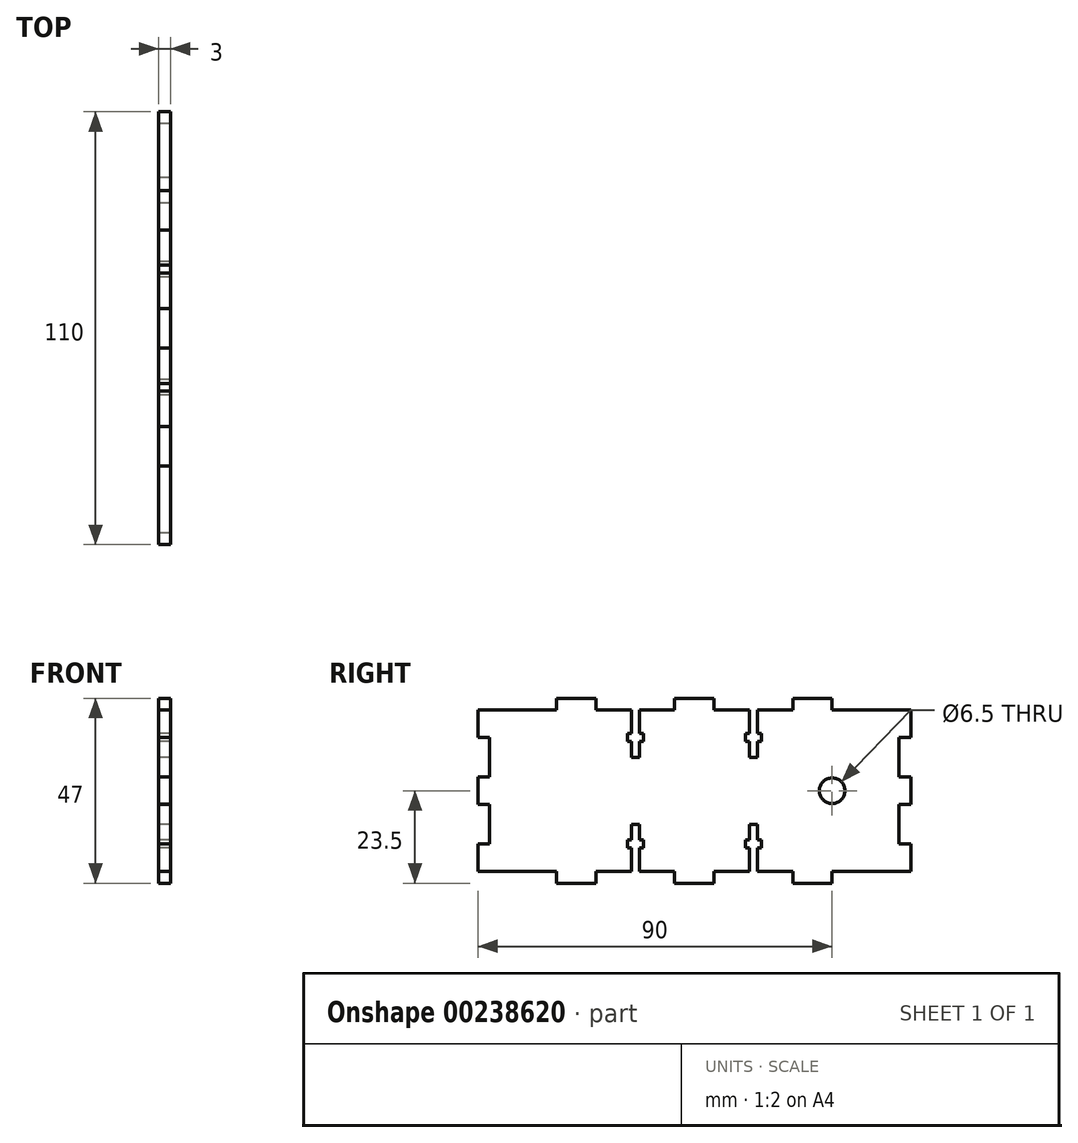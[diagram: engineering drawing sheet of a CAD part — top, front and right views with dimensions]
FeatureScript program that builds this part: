
annotation { "Feature Type Name" : "Feature", "Feature Type Description" : "" }
export const myFeature = defineFeature(function(context is Context, id is Id, definition is map)
    precondition{}
    {
        {
            var Q0;
            Q0=qCreatedBy(makeId("Right.planeOp"),FACE);
            var sketch = newSketch(context, id + "F0", { "sketchPlane" : qUnion([Q0])});
            skLineSegment(sketch, "E0", {"start": v(0, 0) * mm, "end": v(0, 3) * mm});
            skLineSegment(sketch, "E1", {"start": v(0, 3) * mm, "end": v(17, 3) * mm});
            skLineSegment(sketch, "E2", {"start": v(17, 3) * mm, "end": v(17, 10) * mm});
            skLineSegment(sketch, "E3", {"start": v(17, 10) * mm, "end": v(14, 10) * mm});
            skLineSegment(sketch, "E4", {"start": v(14, 10) * mm, "end": v(14, 20) * mm});
            skLineSegment(sketch, "E5", {"start": v(14, 20) * mm, "end": v(17, 20) * mm});
            skLineSegment(sketch, "E6", {"start": v(17, 20) * mm, "end": v(17, 27) * mm});
            skLineSegment(sketch, "E7", {"start": v(17, 27) * mm, "end": v(14, 27) * mm});
            skLineSegment(sketch, "E8", {"start": v(14, 27) * mm, "end": v(14, 37) * mm});
            skLineSegment(sketch, "E9", {"start": v(14, 37) * mm, "end": v(17, 37) * mm});
            skLineSegment(sketch, "E10", {"start": v(17, 37) * mm, "end": v(17, 44) * mm});
            skLineSegment(sketch, "E11", {"start": v(17, 44) * mm, "end": v(-3, 44) * mm});
            skLineSegment(sketch, "E12", {"start": v(-3, 44) * mm, "end": v(-3, 47) * mm});
            skLineSegment(sketch, "E13", {"start": v(-3, 47) * mm, "end": v(-13, 47) * mm});
            skLineSegment(sketch, "E14", {"start": v(-13, 47) * mm, "end": v(-13, 44) * mm});
            skLineSegment(sketch, "E15", {"start": v(-13, 44) * mm, "end": v(-22, 44) * mm});
            skLineSegment(sketch, "E16", {"start": v(-33, 44) * mm, "end": v(-33, 47) * mm});
            skLineSegment(sketch, "E17", {"start": v(-33, 47) * mm, "end": v(-43, 47) * mm});
            skLineSegment(sketch, "E18", {"start": v(-43, 47) * mm, "end": v(-43, 44) * mm});
            skLineSegment(sketch, "E19", {"start": v(-43, 44) * mm, "end": v(-52, 44) * mm});
            skLineSegment(sketch, "E20", {"start": v(-63, 44) * mm, "end": v(-63, 47) * mm});
            skLineSegment(sketch, "E21", {"start": v(-63, 47) * mm, "end": v(-73, 47) * mm});
            skLineSegment(sketch, "E22", {"start": v(-73, 47) * mm, "end": v(-73, 44) * mm});
            skLineSegment(sketch, "E23", {"start": v(-73, 44) * mm, "end": v(-93, 44) * mm});
            skLineSegment(sketch, "E24", {"start": v(17, 23.5) * mm, "end": v(-102.63, 23.5) * mm, "construction": true});
            skLineSegment(sketch, "E25.MirrorCS", {"start": v(-33, 3) * mm, "end": v(-33, 0) * mm});
            skLineSegment(sketch, "E26.MirrorCS", {"start": v(-43, 0) * mm, "end": v(-43, 3) * mm});
            skLineSegment(sketch, "E27.MirrorCS", {"start": v(-63, 3) * mm, "end": v(-63, 0) * mm});
            skLineSegment(sketch, "E28.MirrorCS", {"start": v(-73, 0) * mm, "end": v(-73, 3) * mm});
            skLineSegment(sketch, "E29.MirrorCS", {"start": v(-3, 3) * mm, "end": v(-3, 0) * mm});
            skLineSegment(sketch, "E30.MirrorCS", {"start": v(-13, 0) * mm, "end": v(-13, 3) * mm});
            skLineSegment(sketch, "E31.MirrorCS", {"start": v(17, 3) * mm, "end": v(-3, 3) * mm});
            skLineSegment(sketch, "E32.MirrorCS", {"start": v(-63, 0) * mm, "end": v(-73, 0) * mm});
            skLineSegment(sketch, "E33.MirrorCS", {"start": v(-43, 3) * mm, "end": v(-52, 3) * mm});
            skLineSegment(sketch, "E34.MirrorCS", {"start": v(-73, 3) * mm, "end": v(-93, 3) * mm});
            skLineSegment(sketch, "E35.MirrorCS", {"start": v(-3, 0) * mm, "end": v(-13, 0) * mm});
            skLineSegment(sketch, "E36.MirrorCS", {"start": v(-13, 3) * mm, "end": v(-22, 3) * mm});
            skLineSegment(sketch, "E37.MirrorCS", {"start": v(-33, 0) * mm, "end": v(-43, 0) * mm});
            skLineSegment(sketch, "E38", {"start": v(-38, 47) * mm, "end": v(-38, 0) * mm, "construction": true});
            skLineSegment(sketch, "E39.MirrorCS", {"start": v(-90, 37) * mm, "end": v(-93, 37) * mm});
            skLineSegment(sketch, "E40.MirrorCS", {"start": v(-93, 27) * mm, "end": v(-90, 27) * mm});
            skLineSegment(sketch, "E41.MirrorCS", {"start": v(-90, 20) * mm, "end": v(-93, 20) * mm});
            skLineSegment(sketch, "E42.MirrorCS", {"start": v(-93, 10) * mm, "end": v(-90, 10) * mm});
            skLineSegment(sketch, "E43.MirrorCS", {"start": v(-93, 20) * mm, "end": v(-93, 27) * mm});
            skLineSegment(sketch, "E44.MirrorCS", {"start": v(-90, 27) * mm, "end": v(-90, 37) * mm});
            skLineSegment(sketch, "E45.MirrorCS", {"start": v(-93, 37) * mm, "end": v(-93, 44) * mm});
            skLineSegment(sketch, "E46.MirrorCS", {"start": v(-93, 3) * mm, "end": v(-93, 10) * mm});
            skLineSegment(sketch, "E47.MirrorCS", {"start": v(-90, 10) * mm, "end": v(-90, 20) * mm});
            skLineSegment(sketch, "E48", {"start": v(-23, 44) * mm, "end": v(-23, 38) * mm, "construction": true});
            skLineSegment(sketch, "E49.left", {"start": v(-24, 44) * mm, "end": v(-24, 38) * mm});
            skLineSegment(sketch, "E49.right", {"start": v(-22, 44) * mm, "end": v(-22, 38) * mm});
            skLineSegment(sketch, "E50.trimOffspring", {"start": v(-24, 44) * mm, "end": v(-33, 44) * mm});
            skLineSegment(sketch, "E51.bottom", {"start": v(-25, 38) * mm, "end": v(-24, 38) * mm});
            skLineSegment(sketch, "E51.top", {"start": v(-25, 36) * mm, "end": v(-24, 36) * mm});
            skLineSegment(sketch, "E51.left", {"start": v(-25, 38) * mm, "end": v(-25, 36) * mm});
            skLineSegment(sketch, "E51.right", {"start": v(-21, 38) * mm, "end": v(-21, 36) * mm});
            skLineSegment(sketch, "E52.trimOffspring", {"start": v(-22, 38) * mm, "end": v(-21, 38) * mm});
            skLineSegment(sketch, "E53.trimOffspring", {"start": v(-24, 36) * mm, "end": v(-24, 32) * mm});
            skLineSegment(sketch, "E54.trimOffspring", {"start": v(-22, 36) * mm, "end": v(-21, 36) * mm});
            skLineSegment(sketch, "E55.trimOffspring", {"start": v(-23, 36) * mm, "end": v(-23, 13.38) * mm, "construction": true});
            skLineSegment(sketch, "E56.trimOffspring", {"start": v(-22, 36) * mm, "end": v(-22, 32) * mm});
            skLineSegment(sketch, "E57.MirrorCS", {"start": v(-51, 36) * mm, "end": v(-52, 36) * mm});
            skLineSegment(sketch, "E58.MirrorCS", {"start": v(-54, 38) * mm, "end": v(-55, 38) * mm});
            skLineSegment(sketch, "E59.MirrorCS", {"start": v(-51, 38) * mm, "end": v(-51, 36) * mm});
            skLineSegment(sketch, "E60.MirrorCS", {"start": v(-54, 36) * mm, "end": v(-55, 36) * mm});
            skLineSegment(sketch, "E61.MirrorCS", {"start": v(-51, 38) * mm, "end": v(-52, 38) * mm});
            skLineSegment(sketch, "E62.MirrorCS", {"start": v(-55, 38) * mm, "end": v(-55, 36) * mm});
            skLineSegment(sketch, "E63.MirrorCS", {"start": v(-52, 44) * mm, "end": v(-52, 38) * mm});
            skLineSegment(sketch, "E64.MirrorCS", {"start": v(-54, 44) * mm, "end": v(-54, 38) * mm});
            skLineSegment(sketch, "E65.MirrorCS", {"start": v(-54, 36) * mm, "end": v(-54, 32) * mm});
            skLineSegment(sketch, "E66.MirrorCS", {"start": v(-53, 44) * mm, "end": v(-53, 38) * mm, "construction": true});
            skLineSegment(sketch, "E67.MirrorCS", {"start": v(-52, 36) * mm, "end": v(-52, 32) * mm});
            skLineSegment(sketch, "E68", {"start": v(-24, 32) * mm, "end": v(-22, 32) * mm});
            skLineSegment(sketch, "E69", {"start": v(-54, 32) * mm, "end": v(-52, 32) * mm});
            skLineSegment(sketch, "E70.trimOffspring", {"start": v(-54, 44) * mm, "end": v(-63, 44) * mm});
            skLineSegment(sketch, "E71.MirrorCS", {"start": v(-22, 11) * mm, "end": v(-21, 11) * mm});
            skLineSegment(sketch, "E72.MirrorCS", {"start": v(-51, 9) * mm, "end": v(-52, 9) * mm});
            skLineSegment(sketch, "E73.MirrorCS", {"start": v(-22, 9) * mm, "end": v(-21, 9) * mm});
            skLineSegment(sketch, "E74.MirrorCS", {"start": v(-21, 9) * mm, "end": v(-21, 11) * mm});
            skLineSegment(sketch, "E75.MirrorCS", {"start": v(-55, 9) * mm, "end": v(-55, 11) * mm});
            skLineSegment(sketch, "E76.MirrorCS", {"start": v(-54, 15) * mm, "end": v(-52, 15) * mm});
            skLineSegment(sketch, "E77.MirrorCS", {"start": v(-25, 9) * mm, "end": v(-25, 11) * mm});
            skLineSegment(sketch, "E78.MirrorCS", {"start": v(-51, 9) * mm, "end": v(-51, 11) * mm});
            skLineSegment(sketch, "E79.MirrorCS", {"start": v(-54, 11) * mm, "end": v(-55, 11) * mm});
            skLineSegment(sketch, "E80.MirrorCS", {"start": v(-25, 9) * mm, "end": v(-24, 9) * mm});
            skLineSegment(sketch, "E81.MirrorCS", {"start": v(-24, 15) * mm, "end": v(-22, 15) * mm});
            skLineSegment(sketch, "E82.MirrorCS", {"start": v(-51, 11) * mm, "end": v(-52, 11) * mm});
            skLineSegment(sketch, "E83.MirrorCS", {"start": v(-54, 9) * mm, "end": v(-55, 9) * mm});
            skLineSegment(sketch, "E84.MirrorCS", {"start": v(-25, 11) * mm, "end": v(-24, 11) * mm});
            skLineSegment(sketch, "E85.MirrorCS", {"start": v(-52, 3) * mm, "end": v(-52, 9) * mm});
            skLineSegment(sketch, "E86.MirrorCS", {"start": v(-24, 3) * mm, "end": v(-33, 3) * mm});
            skLineSegment(sketch, "E87.MirrorCS", {"start": v(-22, 3) * mm, "end": v(-22, 9) * mm});
            skLineSegment(sketch, "E88.MirrorCS", {"start": v(-24, 11) * mm, "end": v(-24, 15) * mm});
            skLineSegment(sketch, "E89.MirrorCS", {"start": v(-53, 3) * mm, "end": v(-53, 9) * mm, "construction": true});
            skLineSegment(sketch, "E90.MirrorCS", {"start": v(-23, 3) * mm, "end": v(-23, 9) * mm, "construction": true});
            skLineSegment(sketch, "E91.MirrorCS", {"start": v(-24, 3) * mm, "end": v(-24, 9) * mm});
            skLineSegment(sketch, "E92.MirrorCS", {"start": v(-54, 3) * mm, "end": v(-54, 9) * mm});
            skLineSegment(sketch, "E93.MirrorCS", {"start": v(-22, 11) * mm, "end": v(-22, 15) * mm});
            skLineSegment(sketch, "E94.MirrorCS", {"start": v(-52, 11) * mm, "end": v(-52, 15) * mm});
            skLineSegment(sketch, "E95.MirrorCS", {"start": v(-54, 11) * mm, "end": v(-54, 15) * mm});
            skLineSegment(sketch, "E96.trimOffspring", {"start": v(-54, 3) * mm, "end": v(-63, 3) * mm});
            skCircle(sketch, "E97", {"center": v(-3, 23.5) * mm, "radius": 3.25 * mm});
            skSolve(sketch);
        }
        {
            var Q0;
            Q0 = qSketchRegion(id + "F0", true);
            extrude(context, id + "F1", {"entities" : qUnion([Q0]), "depth" : 3 * mm});
        }
    });
